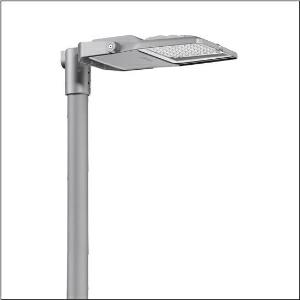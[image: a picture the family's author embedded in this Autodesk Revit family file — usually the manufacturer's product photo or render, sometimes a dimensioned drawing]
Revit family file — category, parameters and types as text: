
# Revit family: floodlight_fl_21_iq_mini___pl61_5xa7771c4c3a_1011
name_source: partatom
category: Lighting Fixtures
units: mm (PartAtom-declared; Revit-internal decimal feet)

## family parameters
Cut with Voids When Loaded = No
Host = Face
Light Source = No
Part Type = Normal
Room Calculation Point = No
Round Connector Dimension = Use Diameter
Shared = No

## types (1)
- --- (1 x LED, 12490 lm, 87.2 W, 4000K)
    Apparent Load = 87 VA
    CIE Flux Codes = 33 65 98 100 100
    Color Rendering = 70
    Color Temperature = 4000K
    Default Elevation = 1800 mm
    Description = Floodlight FL 21 iQ mini, floodlight, primary light control with lens, of PMMA, primary optical cover: protective disc, of toughened safety glass, transparent, light distribution: PL61, light emission: direct distribution, installation type: surface-mounted, lamps: LED, High Power LED, rated values: 12.490lm | 87,2W | 143,2lm/W (begin service life); end service life: 12.490lm | 92,1W; at 50% lumin. flux: 6.245lm | 40,2W | 155,3lm/W, colour temperature: 4000K, colour rendering: CRI > 70, light colour: 740, light setting 1 begin service life: 100% | 12.490lm | 87,2W | 143,2lm/W | 4.000K, light setting 1 end service life: 92,1W, further light settings possible, control: Auto-Match, Temp-Guard, Lumen-Switch, Night-Set, Smart-Wire, Light-Fading, Desk-Remote (wireless, voltage-free reading and setting of iQ features in the workshop via application-optimized NFC function/RFID function), optimised constant luminous flux control (CLO 2.0), pre-setting: linear dimming characteristic, with terminal, 6-pole, mains connection: 220..240V, AC, 50/60Hz, luminaire housing, of diecast aluminium, powder-coated, SITECO metallic grey (DB 702S), corrosivity category C5 mid according to DIN EN ISO 12944suitable for swimming poolschlorine-resistant, sealing non-destructively replaceable, please order mast flange separately, mast bracket, of steel, galvanised, powder-coated, SITECO metallic grey (DB 702S), protection rating (complete): IP66, insulation class (complete): insulation class II (safety insulation), certification: CE, ENEC, VDE, protection symbol: D, impact resistance: IK08, permissible operating ambient temperature: -40..+40°C, permissible operating ambient temperature for outdoor applications: -40..+50°C, standard: DIN EN 12944, LABS conformity tested according to VDMA 24364:2018-05, packaging unit: 1 piece

Light Distribution: PL61
    Height = 70 mm
    Lamp = 1 x LED
    Lamp Light Flux = 12490 lm
    Lamp Power = 87.2 W
    Lamp count = 1
    Length = 485 mm
    Luminous efficacy = 143 lm/W
    Manufacturer = Siteco
    ModVariant = No
    Model = 5XA7771C4C3A
    Mounting Place = Pole
    Mounting Type = Pole annexe
    Number of Poles = 1
    OnlyDefault = Yes
    Power Factor = 1
    Product Name = Floodlight FL 21 iQ mini | PL61
    Product group = floodlight | pylon annexe
    ProductGroupID = 6201
    Protection Class = Protection class II
    Protection Degree = IP 66
    RLX_Detail_Level = 1
    RLX_Emergency_Light_Flux = 0 lm
    RLX_Emergency_Type = 0
    RLX_Emergency_Type_DB = No
    RlxData = <blob elided: 101621 chars, md5=867f67bd>
    Socket = socket
    Standby Power = 0 W
    System Light Flux = 12490 lm
    System Power = 87 W
    Type Comments = factory setting: luminous flux: 100 % | dim-lin: 254 | 456 mA
    Type Image = l_1007125.jpg
    URL = http://relux.com
    VarID = @adj_174229
    Voltage = 0 V
    Weight = 0.00 kg
    Width = 337 mm

## geometry (parser evidence)
native form markers: Blend x4, Sweep x13
no freeform markers — native parametric forms only
